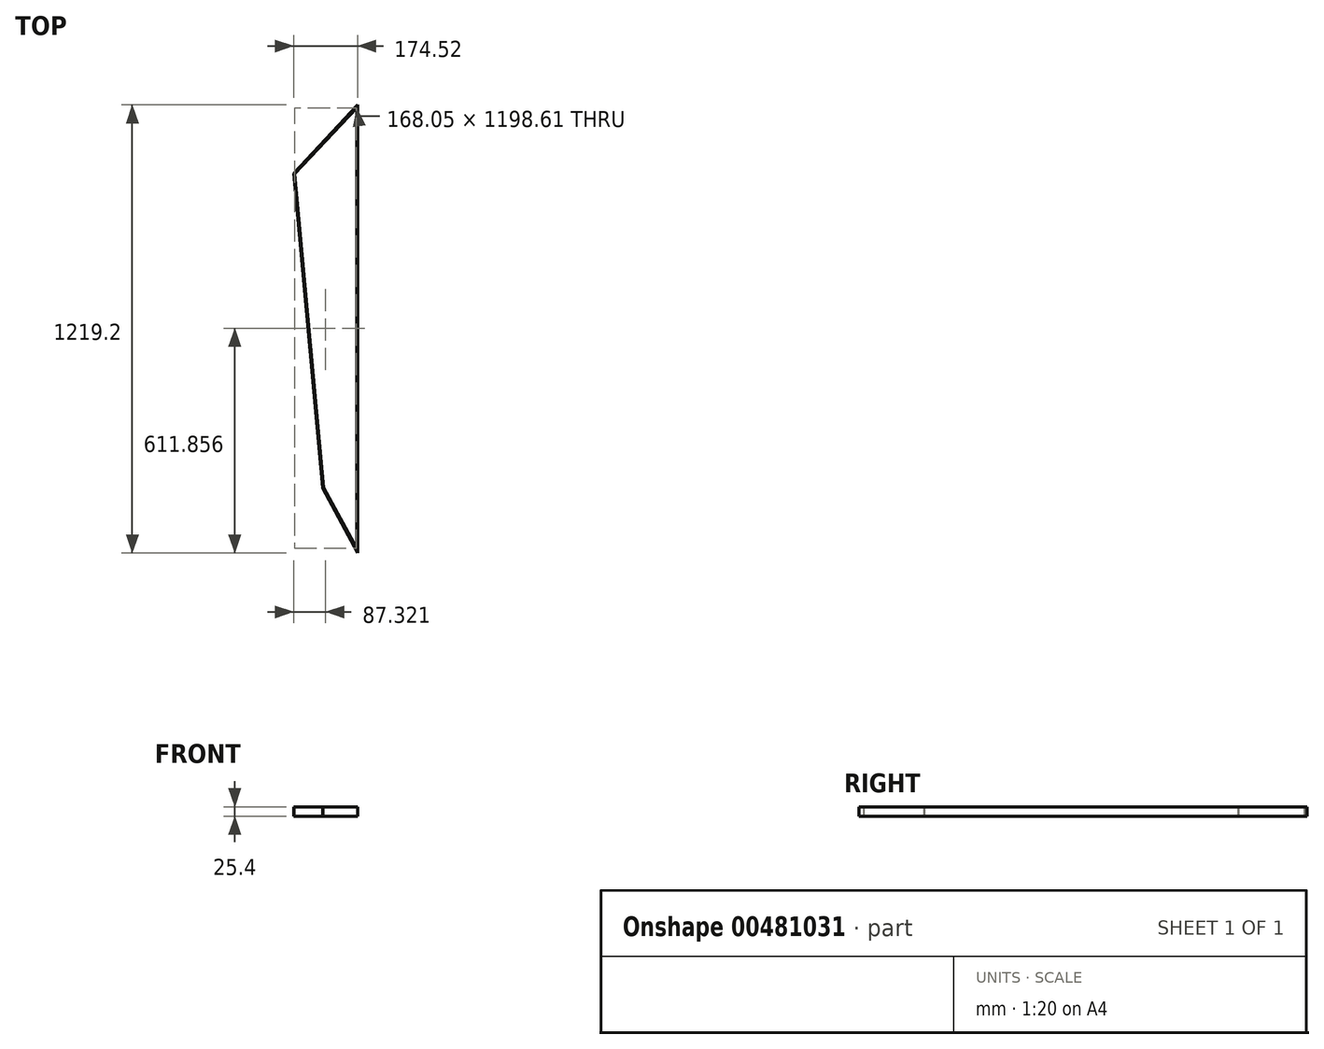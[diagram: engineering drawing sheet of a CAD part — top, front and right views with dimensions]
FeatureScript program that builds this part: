
annotation { "Feature Type Name" : "Feature", "Feature Type Description" : "" }
export const myFeature = defineFeature(function(context is Context, id is Id, definition is map)
    precondition{}
    {
        {
            var Q0;
            Q0=qCreatedBy(makeId("Top.planeOp"),FACE);
            var sketch = newSketch(context, id + "F0", { "sketchPlane" : qUnion([Q0])});
            skLineSegment(sketch, "E0", {"start": v(0, 0) * mm, "end": v(0, 1219.2) * mm});
            skLineSegment(sketch, "E1", {"start": v(0, 1219.2) * mm, "end": v(-174.52, 1032.76) * mm});
            skLineSegment(sketch, "E2", {"start": v(-174.52, 1032.76) * mm, "end": v(-95.54, 176.72) * mm});
            skLineSegment(sketch, "E3", {"start": v(-95.54, 176.72) * mm, "end": v(0, 0) * mm});
            skLineSegment(sketch, "E4.0", {"start": v(-3.18, 1211.16) * mm, "end": v(-171.22, 1031.63) * mm});
            skLineSegment(sketch, "E4.1", {"start": v(-3.18, 12.55) * mm, "end": v(-3.18, 1211.16) * mm});
            skLineSegment(sketch, "E4.2", {"start": v(-92.43, 177.65) * mm, "end": v(-3.18, 12.55) * mm});
            skLineSegment(sketch, "E4.3", {"start": v(-171.22, 1031.63) * mm, "end": v(-92.43, 177.65) * mm});
            skSolve(sketch);
        }
        {
            var Q0;
            Q0 = qSketchRegion(id + "F0", true);
            extrude(context, id + "F1", {"entities" : qUnion([Q0]), "depth" : 25.4 * mm});
        }
        {
            var Q0;
            Q0=makeQuery(id+"F1.opExtrude","CAP_FACE",FACE,{"disambiguationData":[OSD([sQuery(id+"F0.wireOp",EDGE,"E0"),sQuery(id+"F0.wireOp",EDGE,"E1"),sQuery(id+"F0.wireOp",EDGE,"E2"),sQuery(id+"F0.wireOp",EDGE,"E3"),sQuery(id+"F0.wireOp",EDGE,"E4.0"),sQuery(id+"F0.wireOp",EDGE,"E4.1"),sQuery(id+"F0.wireOp",EDGE,"E4.2"),sQuery(id+"F0.wireOp",EDGE,"E4.3")])],"isStart":false});
            var sketch = newSketch(context, id + "F2", { "sketchPlane" : qUnion([Q0])});
            skLineSegment(sketch, "E5", {"start": v(-163.89, 952.13) * mm, "end": v(-3.18, 1123.82) * mm});
            skLineSegment(sketch, "E6", {"start": v(-159.2, 901.38) * mm, "end": v(-3.18, 1068.07) * mm});
            skLineSegment(sketch, "E7", {"start": v(-154.52, 850.62) * mm, "end": v(-3.17, 1012.31) * mm});
            skLineSegment(sketch, "E8", {"start": v(-149.84, 799.87) * mm, "end": v(-3.18, 956.56) * mm});
            skLineSegment(sketch, "E9", {"start": v(-145.16, 749.12) * mm, "end": v(-3.17, 900.8) * mm});
            skLineSegment(sketch, "E10", {"start": v(-140.48, 698.37) * mm, "end": v(-3.18, 845.06) * mm});
            skLineSegment(sketch, "E11", {"start": v(-135.8, 647.62) * mm, "end": v(-3.18, 789.3) * mm});
            skLineSegment(sketch, "E12", {"start": v(-131.11, 596.87) * mm, "end": v(-3.18, 733.55) * mm});
            skLineSegment(sketch, "E13", {"start": v(-126.43, 546.12) * mm, "end": v(-3.18, 677.8) * mm});
            skSolve(sketch);
        }
        {
            var Q0;
            Q0 = qSketchRegion(id + "F2", true);
            var Q1;
            Q1=sQuery(id+"F2.wireOp",EDGE,"E5");
            var Q2;
            Q2=sQuery(id+"F2.wireOp",EDGE,"E6");
            var Q3;
            Q3=sQuery(id+"F2.wireOp",EDGE,"E7");
            var Q4;
            Q4=sQuery(id+"F2.wireOp",EDGE,"E8");
            var Q5;
            Q5=sQuery(id+"F2.wireOp",EDGE,"E9");
            var Q6;
            Q6=sQuery(id+"F2.wireOp",EDGE,"E10");
            var Q7;
            Q7=sQuery(id+"F2.wireOp",EDGE,"E11");
            var Q8;
            Q8=sQuery(id+"F2.wireOp",EDGE,"E12");
            var Q9;
            Q9=sQuery(id+"F2.wireOp",EDGE,"E13");
            extrude(context, id + "F3", {"entities" : qUnion([Q0]), "bodyType" : ToolBodyType.SURFACE, "surfaceEntities" : qUnion([Q1, Q2, Q3, Q4, Q5, Q6, Q7, Q8, Q9]), "oppositeDirection" : true, "depth" : 25.4 * mm});
        }
    });
